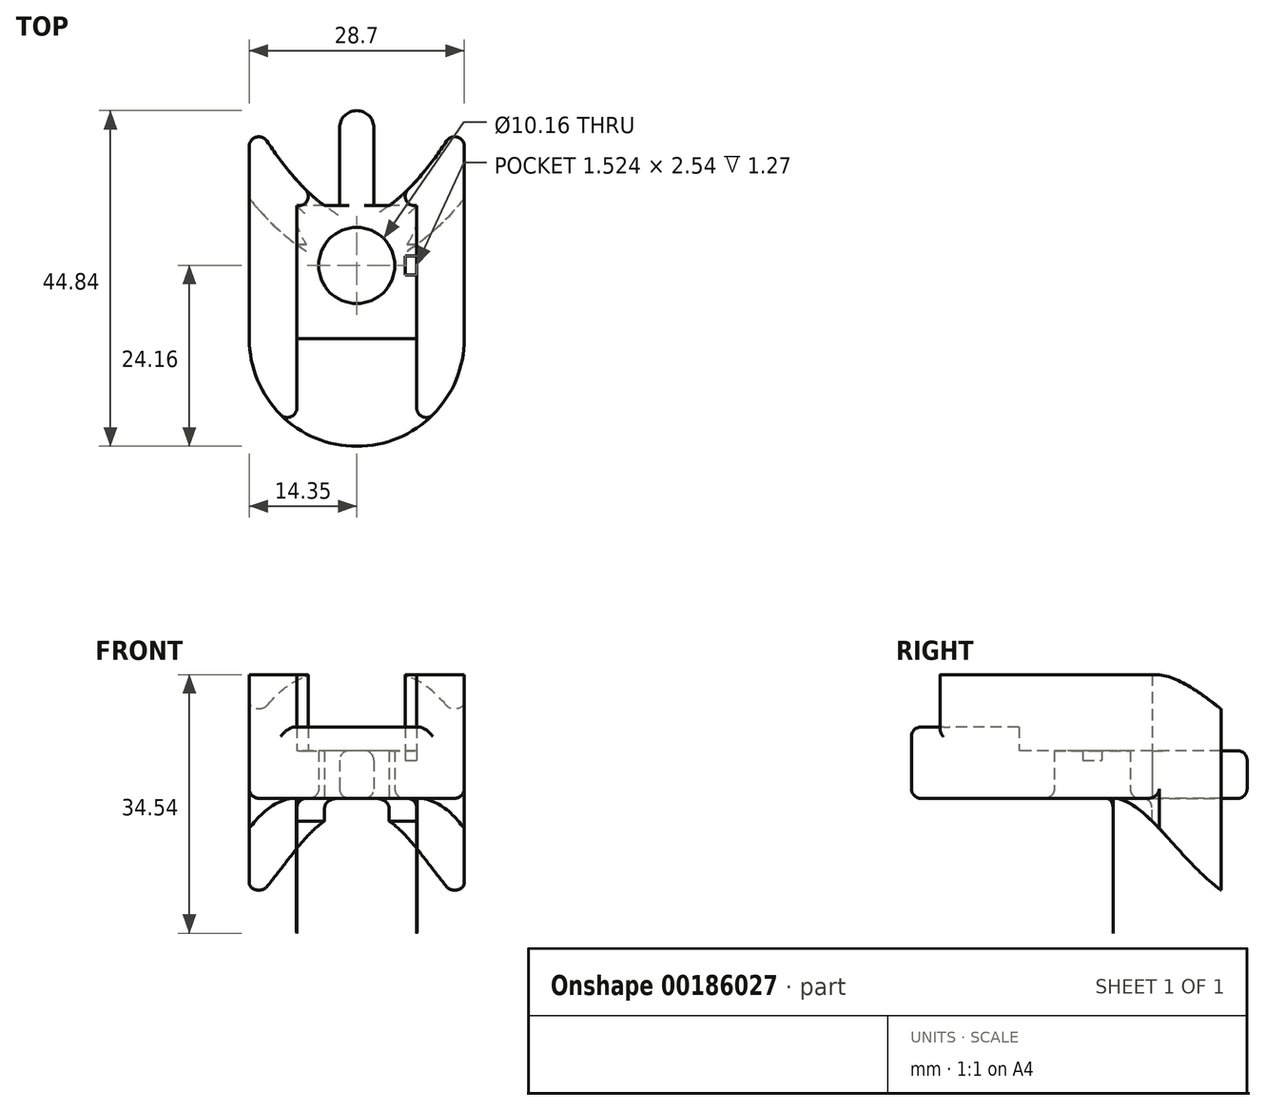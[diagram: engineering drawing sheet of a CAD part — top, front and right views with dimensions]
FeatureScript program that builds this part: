
annotation { "Feature Type Name" : "Feature", "Feature Type Description" : "" }
export const myFeature = defineFeature(function(context is Context, id is Id, definition is map)
    precondition{}
    {
        {
            var Q0;
            Q0=qCreatedBy(makeId("Top.planeOp"),FACE);
            var sketch = newSketch(context, id + "F0", { "sketchPlane" : qUnion([Q0])});
            skLineSegment(sketch, "E0", {"start": v(0, 45.72) * mm, "end": v(0, -45.72) * mm, "construction": true});
            skLineSegment(sketch, "E1", {"start": v(-22.35, 22.86) * mm, "end": v(22.35, 22.86) * mm, "construction": true});
            skLineSegment(sketch, "E2", {"start": v(-18.8, -22.86) * mm, "end": v(18.8, -22.86) * mm, "construction": true});
            skPoint(sketch, "E3", {"position": v(0, 22.86) * mm});
            skPoint(sketch, "E4", {"position": v(0, -22.86) * mm});
            skPoint(sketch, "E5", {"position": v(0, 0) * mm});
            skLineSegment(sketch, "E6", {"start": v(-24, 0) * mm, "end": v(24, 0) * mm, "construction": true});
            skFitSpline(sketch, "E7", {"points": [v(0, 45.72) * mm, v(-22.35, 22.86) * mm, v(-24, 0) * mm, v(-18.8, -22.86) * mm, v(0, -45.72) * mm], "startDerivative": vector(-139.64, 0) * mm, "endDerivative": vector(72.57, 0) * mm});
            skLineSegment(sketch, "E8", {"start": v(0, -45.72) * mm, "end": v(-6.35, -45.72) * mm, "construction": true});
            skLineSegment(sketch, "E9", {"start": v(-12.7, 45.72) * mm, "end": v(0, 45.72) * mm});
            skFitSpline(sketch, "E10.MirrorCS", {"points": [v(0, 45.72) * mm, v(22.35, 22.86) * mm, v(24, 0) * mm, v(18.8, -22.86) * mm, v(0, -45.72) * mm], "startDerivative": vector(139.64, 0) * mm, "endDerivative": vector(-72.57, 0) * mm});
            skFitSpline(sketch, "E11.0", {"points": [v(0, 52.07) * mm, v(-1.93, 52.07) * mm, v(-5.68, 51.63) * mm, v(-10.74, 49.77) * mm, v(-15.08, 47) * mm, v(-18.7, 43.6) * mm, v(-21.67, 39.8) * mm, v(-24.1, 35.77) * mm, v(-26.06, 31.63) * mm, v(-27.36, 28.19) * mm, v(-28.21, 25.5) * mm, v(-28.95, 22.86) * mm, v(-29.67, 19.67) * mm, v(-30.26, 16) * mm, v(-30.6, 12.49) * mm, v(-30.74, 9.12) * mm, v(-30.71, 5.9) * mm, v(-30.6, 3.32) * mm, v(-30.47, 1.33) * mm, v(-30.38, 0.1) * mm, v(-30.3, -0.86) * mm, v(-30.23, -1.83) * mm, v(-30.12, -3.05) * mm, v(-29.98, -4.54) * mm, v(-29.75, -6.56) * mm, v(-29.4, -9.16) * mm, v(-28.8, -12.4) * mm, v(-28, -15.78) * mm, v(-26.96, -19.32) * mm, v(-25.85, -22.4) * mm, v(-24.81, -24.96) * mm, v(-23.66, -27.59) * mm, v(-22.04, -30.96) * mm, v(-19.82, -35.02) * mm, v(-17.37, -38.97) * mm, v(-14.71, -42.67) * mm, v(-12.32, -45.47) * mm, v(-10.26, -47.47) * mm, v(-8.62, -48.84) * mm, v(-6.83, -50.07) * mm, v(-4.85, -51.1) * mm, v(-2.6, -51.86) * mm, v(-0.88, -52.07) * mm, v(0, -52.07) * mm]});
            skFitSpline(sketch, "E11.1", {"points": [v(0, 52.07) * mm, v(1.93, 52.07) * mm, v(5.68, 51.63) * mm, v(10.74, 49.77) * mm, v(15.08, 47) * mm, v(18.7, 43.6) * mm, v(21.67, 39.8) * mm, v(24.1, 35.77) * mm, v(26.06, 31.63) * mm, v(27.36, 28.19) * mm, v(28.21, 25.5) * mm, v(28.95, 22.86) * mm, v(29.67, 19.67) * mm, v(30.26, 16) * mm, v(30.6, 12.49) * mm, v(30.74, 9.12) * mm, v(30.71, 5.9) * mm, v(30.6, 3.32) * mm, v(30.47, 1.33) * mm, v(30.38, 0.1) * mm, v(30.3, -0.86) * mm, v(30.23, -1.83) * mm, v(30.12, -3.05) * mm, v(29.98, -4.54) * mm, v(29.75, -6.56) * mm, v(29.4, -9.16) * mm, v(28.8, -12.4) * mm, v(28, -15.78) * mm, v(26.96, -19.32) * mm, v(25.85, -22.4) * mm, v(24.81, -24.96) * mm, v(23.66, -27.59) * mm, v(22.04, -30.96) * mm, v(19.82, -35.02) * mm, v(17.37, -38.97) * mm, v(14.71, -42.67) * mm, v(12.32, -45.47) * mm, v(10.26, -47.47) * mm, v(8.62, -48.84) * mm, v(6.83, -50.07) * mm, v(4.85, -51.1) * mm, v(2.6, -51.86) * mm, v(0.88, -52.07) * mm, v(0, -52.07) * mm]});
            skLineSegment(sketch, "E12", {"start": v(-22.35, 22.86) * mm, "end": v(-30.27, 15.58) * mm});
            skLineSegment(sketch, "E13.MirrorCS", {"start": v(22.35, 22.86) * mm, "end": v(30.27, 15.58) * mm});
            skLineSegment(sketch, "E14.bottom", {"start": v(8, -44.1) * mm, "end": v(-8, -44.1) * mm});
            skLineSegment(sketch, "E14.top", {"start": v(8, -61.87) * mm, "end": v(-8, -61.87) * mm});
            skLineSegment(sketch, "E14.left", {"start": v(8, -44.1) * mm, "end": v(8, -61.87) * mm});
            skLineSegment(sketch, "E14.right", {"start": v(-8, -44.1) * mm, "end": v(-8, -61.87) * mm});
            skPoint(sketch, "E14.middle", {"position": v(0, -52.98) * mm});
            skCircle(sketch, "E15", {"center": v(0, -52.07) * mm, "radius": 5.08 * mm});
            skLineSegment(sketch, "E16", {"start": v(14.35, -31.7) * mm, "end": v(14.35, -61.87) * mm});
            skLineSegment(sketch, "E17", {"start": v(14.35, -61.87) * mm, "end": v(-14.35, -61.87) * mm, "construction": true});
            skLineSegment(sketch, "E18", {"start": v(-14.35, -61.87) * mm, "end": v(-14.35, -31.7) * mm});
            skArc(sketch, "E19", {"start": v(-14.35, -61.87) * mm, "mid": v(0, -76.23) * mm, "end": v(14.35, -61.87) * mm});
            skLineSegment(sketch, "E20", {"start": v(8, -61.87) * mm, "end": v(8, -73.79) * mm});
            skLineSegment(sketch, "E21", {"start": v(-8, -61.87) * mm, "end": v(-8, -73.79) * mm});
            skLineSegment(sketch, "E22", {"start": v(-2.29, -44.1) * mm, "end": v(-2.29, -33.68) * mm});
            skArc(sketch, "E23", {"start": v(-2.29, -33.68) * mm, "mid": v(0, -31.4) * mm, "end": v(2.29, -33.68) * mm});
            skLineSegment(sketch, "E24", {"start": v(2.29, -33.68) * mm, "end": v(2.29, -44.1) * mm});
            skLineSegment(sketch, "E25", {"start": v(-2.29, -33.68) * mm, "end": v(2.29, -33.68) * mm, "construction": true});
            skLineSegment(sketch, "E26", {"start": v(0, -52.07) * mm, "end": v(8, -52.07) * mm, "construction": true});
            skLineSegment(sketch, "E27.bottom", {"start": v(8, -50.8) * mm, "end": v(6.48, -50.8) * mm});
            skLineSegment(sketch, "E27.top", {"start": v(8, -53.34) * mm, "end": v(6.48, -53.34) * mm});
            skLineSegment(sketch, "E27.left", {"start": v(8, -50.8) * mm, "end": v(8, -53.34) * mm});
            skLineSegment(sketch, "E27.right", {"start": v(6.48, -50.8) * mm, "end": v(6.48, -53.34) * mm});
            skPoint(sketch, "E27.middle", {"position": v(7.24, -52.07) * mm});
            skSolve(sketch);
        }
        {
            var Q0;
            {var subQ0=sQuery(id+"F0.wireOp",EDGE,"E12");var subQ1=sQuery(id+"F0.wireOp",EDGE,"E7");var subQ2=makeQuery(id+"F0.imprint","INTERSECT",VERTEX,{"derivedFrom":[subQ1,subQ0]});Q0=makeQuery(id+"F0.imprint","IMPRINT",FACE,{"disambiguationData":[TD([[makeQuery(id+"F0.imprint","IMPRINT",EDGE,{"disambiguationData":[TD([[subQ2,-1.0]])],"derivedFrom":subQ1}),-1.0]])]});}
            var Q1;
            {var subQ3=sQuery(id+"F0.wireOp",EDGE,"E7");var subQ5=sQuery(id+"F0.wireOp",EDGE,"E18");var subQ6=makeQuery(id+"F0.imprint","INTERSECT",VERTEX,{"derivedFrom":[subQ3,subQ5]});Q1=makeQuery(id+"F0.imprint","IMPRINT",FACE,{"disambiguationData":[TD([[makeQuery(id+"F0.imprint","IMPRINT",EDGE,{"disambiguationData":[TD([[subQ6,-1.0]])],"derivedFrom":subQ3}),-1.0]])]});}
            var Q2;
            {var subQ0=sQuery(id+"F0.wireOp",EDGE,"E13.MirrorCS");var subQ1=sQuery(id+"F0.wireOp",EDGE,"E10.MirrorCS");var subQ2=makeQuery(id+"F0.imprint","INTERSECT",VERTEX,{"derivedFrom":[subQ1,subQ0]});Q2=makeQuery(id+"F0.imprint","IMPRINT",FACE,{"disambiguationData":[TD([[makeQuery(id+"F0.imprint","IMPRINT",EDGE,{"disambiguationData":[TD([[subQ2,-1.0]])],"derivedFrom":subQ1}),1.0]])]});}
            var Q3;
            {var subQ5=sQuery(id+"F0.wireOp",EDGE,"E16");var subQ6=sQuery(id+"F0.wireOp",EDGE,"E10.MirrorCS");var subQ7=makeQuery(id+"F0.imprint","INTERSECT",VERTEX,{"derivedFrom":[subQ6,subQ5]});Q3=makeQuery(id+"F0.imprint","IMPRINT",FACE,{"disambiguationData":[TD([[makeQuery(id+"F0.imprint","IMPRINT",EDGE,{"disambiguationData":[TD([[subQ7,-1.0]])],"derivedFrom":subQ6}),1.0]])]});}
            var Q4;
            {var subQ3=sQuery(id+"F0.wireOp",EDGE,"E20");Q4=makeQuery(id+"F0.imprint","IMPRINT",FACE,{"disambiguationData":[TD([[makeQuery(id+"F0.imprint","IMPRINT",EDGE,{"derivedFrom":subQ3}),1.0]])]});}
            var Q5;
            {var subQ3=sQuery(id+"F0.wireOp",EDGE,"E21");Q5=makeQuery(id+"F0.imprint","IMPRINT",FACE,{"disambiguationData":[TD([[makeQuery(id+"F0.imprint","IMPRINT",EDGE,{"derivedFrom":subQ3}),-1.0]])]});}
            var Q6;
            {var subQ5=sQuery(id+"F0.wireOp",EDGE,"E10.MirrorCS");var subQ6=sQuery(id+"F0.wireOp",EDGE,"E7");var subQ7=makeQuery(id+"F0.imprint","INTERSECT",VERTEX,{"disambiguationData":[OD(1.0)],"derivedFrom":[subQ6,subQ5]});Q6=makeQuery(id+"F0.imprint","IMPRINT",FACE,{"disambiguationData":[TD([[makeQuery(id+"F0.imprint","IMPRINT",EDGE,{"disambiguationData":[TD([[subQ7,1.0]])],"derivedFrom":subQ6}),-1.0]])]});}
            var Q7;
            {var subQ0=sQuery(id+"F0.wireOp",EDGE,"E14.top");Q7=makeQuery(id+"F0.imprint","IMPRINT",FACE,{"disambiguationData":[TD([[makeQuery(id+"F0.imprint","IMPRINT",EDGE,{"derivedFrom":subQ0}),-1.0]])]});}
            var Q8;
            Q8=makeQuery(id+"F0.imprint","IMPRINT",FACE,{"disambiguationData":[TD([[makeQuery(id+"F0.imprint","IMPRINT",EDGE,{"derivedFrom":sQuery(id+"F0.wireOp",EDGE,"E14.top")}),1.0]])]});
            var Q9;
            {var subQ0=sQuery(id+"F0.wireOp",EDGE,"E10.MirrorCS");var subQ1=sQuery(id+"F0.wireOp",EDGE,"E7");var subQ2=makeQuery(id+"F0.imprint","INTERSECT",VERTEX,{"disambiguationData":[OD(1.0)],"derivedFrom":[subQ1,subQ0]});Q9=makeQuery(id+"F0.imprint","IMPRINT",FACE,{"disambiguationData":[TD([[makeQuery(id+"F0.imprint","IMPRINT",EDGE,{"disambiguationData":[TD([[subQ2,1.0]])],"derivedFrom":subQ1}),1.0]])]});}
            var Q10;
            {var subQ0=sQuery(id+"F0.wireOp",EDGE,"E22");Q10=makeQuery(id+"F0.imprint","IMPRINT",FACE,{"disambiguationData":[TD([[makeQuery(id+"F0.imprint","IMPRINT",EDGE,{"derivedFrom":subQ0}),-1.0]])]});}
            var Q11;
            Q11=makeQuery(id+"F0.imprint","IMPRINT",FACE,{"disambiguationData":[TD([[makeQuery(id+"F0.imprint","IMPRINT",EDGE,{"derivedFrom":sQuery(id+"F0.wireOp",EDGE,"E27.bottom")}),1.0]])]});
            extrude(context, id + "F1", {"entities" : qUnion([Q0, Q1, Q2, Q3, Q4, Q5, Q6, Q7, Q8, Q9, Q10, Q11]), "depth" : 5.08 * mm});
        }
        {
            var Q0;
            {var subQ7=sQuery(id+"F0.wireOp",EDGE,"E14.top");Q0=makeQuery(id+"F0.imprint","IMPRINT",FACE,{"disambiguationData":[TD([[makeQuery(id+"F0.imprint","IMPRINT",EDGE,{"derivedFrom":subQ7}),-1.0]])]});}
            var Q1;
            {var subQ5=sQuery(id+"F0.wireOp",EDGE,"E10.MirrorCS");var subQ6=sQuery(id+"F0.wireOp",EDGE,"E7");var subQ7=makeQuery(id+"F0.imprint","INTERSECT",VERTEX,{"disambiguationData":[OD(1.0)],"derivedFrom":[subQ6,subQ5]});Q1=makeQuery(id+"F0.imprint","IMPRINT",FACE,{"disambiguationData":[TD([[makeQuery(id+"F0.imprint","IMPRINT",EDGE,{"disambiguationData":[TD([[subQ7,1.0]])],"derivedFrom":subQ6}),-1.0]])]});}
            var Q2;
            {var subQ0=sQuery(id+"F0.wireOp",EDGE,"E22");Q2=makeQuery(id+"F0.imprint","IMPRINT",FACE,{"disambiguationData":[TD([[makeQuery(id+"F0.imprint","IMPRINT",EDGE,{"derivedFrom":subQ0}),-1.0]])]});}
            var Q3;
            {var subQ3=sQuery(id+"F0.wireOp",EDGE,"E7");var subQ5=sQuery(id+"F0.wireOp",EDGE,"E10.MirrorCS");var subQ7=makeQuery(id+"F0.imprint","INTERSECT",VERTEX,{"disambiguationData":[OD(1.0)],"derivedFrom":[subQ3,subQ5]});Q3=makeQuery(id+"F0.imprint","IMPRINT",FACE,{"disambiguationData":[TD([[makeQuery(id+"F0.imprint","IMPRINT",EDGE,{"disambiguationData":[TD([[subQ7,1.0]])],"derivedFrom":subQ3}),1.0]])]});}
            extrude(context, id + "F2", {"entities" : qUnion([Q0, Q1, Q2, Q3]), "operationType" : NewBodyOperationType.ADD, "depth" : 6.35 * mm});
        }
        {
            var Q0;
            Q0=makeQuery(id+"F0.imprint","IMPRINT",FACE,{"disambiguationData":[TD([[makeQuery(id+"F0.imprint","IMPRINT",EDGE,{"derivedFrom":sQuery(id+"F0.wireOp",EDGE,"E14.top")}),1.0]])]});
            extrude(context, id + "F3", {"entities" : qUnion([Q0]), "operationType" : NewBodyOperationType.ADD, "depth" : 9.52 * mm});
        }
        {
            var Q0;
            {var subQ5=sQuery(id+"F0.wireOp",EDGE,"E20");Q0=makeQuery(id+"F0.imprint","IMPRINT",FACE,{"disambiguationData":[TD([[makeQuery(id+"F0.imprint","IMPRINT",EDGE,{"derivedFrom":subQ5}),1.0]])]});}
            var Q1;
            {var subQ5=sQuery(id+"F0.wireOp",EDGE,"E16");var subQ7=sQuery(id+"F0.wireOp",EDGE,"E10.MirrorCS");var subQ9=makeQuery(id+"F0.imprint","INTERSECT",VERTEX,{"derivedFrom":[subQ7,subQ5]});Q1=makeQuery(id+"F0.imprint","IMPRINT",FACE,{"disambiguationData":[TD([[makeQuery(id+"F0.imprint","IMPRINT",EDGE,{"disambiguationData":[TD([[subQ9,-1.0]])],"derivedFrom":subQ7}),1.0]])]});}
            var Q2;
            {var subQ3=sQuery(id+"F0.wireOp",EDGE,"E21");Q2=makeQuery(id+"F0.imprint","IMPRINT",FACE,{"disambiguationData":[TD([[makeQuery(id+"F0.imprint","IMPRINT",EDGE,{"derivedFrom":subQ3}),-1.0]])]});}
            var Q3;
            {var subQ5=sQuery(id+"F0.wireOp",EDGE,"E18");var subQ6=sQuery(id+"F0.wireOp",EDGE,"E7");var subQ7=makeQuery(id+"F0.imprint","INTERSECT",VERTEX,{"derivedFrom":[subQ6,subQ5]});Q3=makeQuery(id+"F0.imprint","IMPRINT",FACE,{"disambiguationData":[TD([[makeQuery(id+"F0.imprint","IMPRINT",EDGE,{"disambiguationData":[TD([[subQ7,-1.0]])],"derivedFrom":subQ6}),-1.0]])]});}
            extrude(context, id + "F4", {"entities" : qUnion([Q0, Q1, Q2, Q3]), "operationType" : NewBodyOperationType.ADD, "depth" : 16.5 * mm});
        }
        {
            var Q0;
            {var subQ5=sQuery(id+"F0.wireOp",EDGE,"E18");var subQ6=sQuery(id+"F0.wireOp",EDGE,"E7");var subQ7=makeQuery(id+"F0.imprint","INTERSECT",VERTEX,{"derivedFrom":[subQ6,subQ5]});Q0=makeQuery(id+"F0.imprint","IMPRINT",FACE,{"disambiguationData":[TD([[makeQuery(id+"F0.imprint","IMPRINT",EDGE,{"disambiguationData":[TD([[subQ7,-1.0]])],"derivedFrom":subQ6}),-1.0]])]});}
            var Q1;
            {var subQ0=sQuery(id+"F0.wireOp",EDGE,"E12");var subQ1=sQuery(id+"F0.wireOp",EDGE,"E7");var subQ2=makeQuery(id+"F0.imprint","INTERSECT",VERTEX,{"derivedFrom":[subQ1,subQ0]});Q1=makeQuery(id+"F0.imprint","IMPRINT",FACE,{"disambiguationData":[TD([[makeQuery(id+"F0.imprint","IMPRINT",EDGE,{"disambiguationData":[TD([[subQ2,-1.0]])],"derivedFrom":subQ1}),-1.0]])]});}
            var Q2;
            {var subQ5=sQuery(id+"F0.wireOp",EDGE,"E16");var subQ7=sQuery(id+"F0.wireOp",EDGE,"E10.MirrorCS");var subQ9=makeQuery(id+"F0.imprint","INTERSECT",VERTEX,{"derivedFrom":[subQ7,subQ5]});Q2=makeQuery(id+"F0.imprint","IMPRINT",FACE,{"disambiguationData":[TD([[makeQuery(id+"F0.imprint","IMPRINT",EDGE,{"disambiguationData":[TD([[subQ9,-1.0]])],"derivedFrom":subQ7}),1.0]])]});}
            var Q3;
            {var subQ0=sQuery(id+"F0.wireOp",EDGE,"E13.MirrorCS");var subQ1=sQuery(id+"F0.wireOp",EDGE,"E10.MirrorCS");var subQ2=makeQuery(id+"F0.imprint","INTERSECT",VERTEX,{"derivedFrom":[subQ1,subQ0]});Q3=makeQuery(id+"F0.imprint","IMPRINT",FACE,{"disambiguationData":[TD([[makeQuery(id+"F0.imprint","IMPRINT",EDGE,{"disambiguationData":[TD([[subQ2,-1.0]])],"derivedFrom":subQ1}),1.0]])]});}
            extrude(context, id + "F5", {"entities" : qUnion([Q0, Q1, Q2, Q3]), "operationType" : NewBodyOperationType.ADD, "oppositeDirection" : true, "depth" : 19.05 * mm, "hasSecondDirection" : true, "secondDirectionOppositeDirection" : false, "secondDirectionDepth" : 16.5 * mm});
        }
        {
            var Q0;
            Q0=qCreatedBy(makeId("Right.planeOp"),FACE);
            var sketch = newSketch(context, id + "F6", { "sketchPlane" : qUnion([Q0])});
            skFitSpline(sketch, "E28", {"points": [v(-49.27, 0) * mm, v(-40.72, -6.68) * mm, v(-32.49, -13.94) * mm, v(-17.05, -19.05) * mm], "startDerivative": vector(27.03, 0) * mm, "endDerivative": vector(45.72, -0.93) * mm});
            skFitSpline(sketch, "E29", {"points": [v(-11.78, 0) * mm, v(-29.9, 7.9) * mm, v(-43.68, 16.51) * mm], "startDerivative": vector(-38.45, 0) * mm, "endDerivative": vector(-24.58, 0) * mm});
            skLineSegment(sketch, "E30", {"start": v(-43.68, 16.51) * mm, "end": v(22.86, 16.51) * mm});
            skLineSegment(sketch, "E31", {"start": v(22.86, 16.51) * mm, "end": v(22.86, 0) * mm});
            skLineSegment(sketch, "E32", {"start": v(22.86, 0) * mm, "end": v(-11.78, 0) * mm});
            skLineSegment(sketch, "E33", {"start": v(-49.27, 0) * mm, "end": v(-49.27, -19.05) * mm});
            skLineSegment(sketch, "E34", {"start": v(-49.27, -19.05) * mm, "end": v(-17.05, -19.05) * mm});
            skSolve(sketch);
        }
        {
            var Q0;
            Q0=makeQuery(id+"F6.imprint","IMPRINT",FACE,{"disambiguationData":[TD([[makeQuery(id+"F6.imprint","IMPRINT",EDGE,{"derivedFrom":sQuery(id+"F6.wireOp",EDGE,"E29")}),-1.0]])]});
            var Q1;
            Q1=makeQuery(id+"F6.imprint","IMPRINT",FACE,{"disambiguationData":[TD([[makeQuery(id+"F6.imprint","IMPRINT",EDGE,{"derivedFrom":sQuery(id+"F6.wireOp",EDGE,"E28")}),-1.0]])]});
            extrude(context, id + "F7", {"entities" : qUnion([Q0, Q1]), "operationType" : NewBodyOperationType.REMOVE, "endBound" : BoundingType.THROUGH_ALL, "oppositeDirection" : true, "depth" : 50.8 * mm, "hasSecondDirection" : true, "secondDirectionBound" : SecondDirectionBoundingType.THROUGH_ALL, "secondDirectionOppositeDirection" : false, "secondDirectionDepth" : 25.4 * mm});
        }
        {
            var Q0;
            {var subQ0=sQuery(id+"F0.wireOp",EDGE,"be17f513-7395-4ca1-bee9-ffb8ea424e3f");Q0=makeQuery(id+"F7.boolean.opBoolean","INTERSECT",EDGE,{"derivedFrom":[makeQuery(id+"F5.boolean.opBoolean","MERGE",FACE,{"derivedFrom":[makeQuery(id+"F4.boolean.opBoolean","MERGE",FACE,{"derivedFrom":[makeQuery(id+"F3.boolean.opBoolean","MERGE",FACE,{"derivedFrom":[makeQuery(id+"F1.opExtrude","SWEPT_FACE",FACE,{"disambiguationData":[OSD([subQ0])]}),makeQuery(id+"F3.opExtrude","SWEPT_FACE",FACE,{"disambiguationData":[OSD([subQ0])]})]}),makeQuery(id+"F4.opExtrude","SWEPT_FACE",FACE,{"disambiguationData":[OSD([subQ0])]})]}),makeQuery(id+"F5.opExtrude","SWEPT_FACE",FACE,{"disambiguationData":[OSD([subQ0])]})]}),makeQuery(id+"F7.opExtrude","SWEPT_FACE",FACE,{"disambiguationData":[OSD([sQuery(id+"F6.wireOp",EDGE,"E29")])]})]});}
            var Q1;
            {var subQ0=sQuery(id+"F0.wireOp",EDGE,"43ab01d4-1301-4dd6-aa0a-0130827a8f120.MirrorCS");Q1=makeQuery(id+"F7.boolean.opBoolean","INTERSECT",EDGE,{"derivedFrom":[makeQuery(id+"F5.boolean.opBoolean","MERGE",FACE,{"derivedFrom":[makeQuery(id+"F4.boolean.opBoolean","MERGE",FACE,{"derivedFrom":[makeQuery(id+"F3.boolean.opBoolean","MERGE",FACE,{"derivedFrom":[makeQuery(id+"F1.opExtrude","SWEPT_FACE",FACE,{"disambiguationData":[OSD([subQ0])]}),makeQuery(id+"F3.opExtrude","SWEPT_FACE",FACE,{"disambiguationData":[OSD([subQ0])]})]}),makeQuery(id+"F4.opExtrude","SWEPT_FACE",FACE,{"disambiguationData":[OSD([subQ0])]})]}),makeQuery(id+"F5.opExtrude","SWEPT_FACE",FACE,{"disambiguationData":[OSD([subQ0])]})]}),makeQuery(id+"F7.opExtrude","SWEPT_FACE",FACE,{"disambiguationData":[OSD([sQuery(id+"F6.wireOp",EDGE,"E29")])]})]});}
            var Q2;
            {var subQ0=sQuery(id+"F0.wireOp",EDGE,"ee3d559f-ee6a-4725-bef5-1b4b77159640.1");Q2=makeQuery(id+"F7.boolean.opBoolean","INTERSECT",EDGE,{"derivedFrom":[makeQuery(id+"F5.boolean.opBoolean","MERGE",FACE,{"derivedFrom":[makeQuery(id+"F1.opExtrude","SWEPT_FACE",FACE,{"disambiguationData":[OSD([subQ0])]}),makeQuery(id+"F5.opExtrude","SWEPT_FACE",FACE,{"disambiguationData":[OSD([subQ0])]})]}),makeQuery(id+"F7.opExtrude","SWEPT_FACE",FACE,{"disambiguationData":[OSD([sQuery(id+"F6.wireOp",EDGE,"E29")])]})]});}
            var Q3;
            {var subQ0=sQuery(id+"F0.wireOp",EDGE,"ee3d559f-ee6a-4725-bef5-1b4b77159640.0");Q3=makeQuery(id+"F7.boolean.opBoolean","INTERSECT",EDGE,{"derivedFrom":[makeQuery(id+"F5.boolean.opBoolean","MERGE",FACE,{"derivedFrom":[makeQuery(id+"F1.opExtrude","SWEPT_FACE",FACE,{"disambiguationData":[OSD([subQ0])]}),makeQuery(id+"F5.opExtrude","SWEPT_FACE",FACE,{"disambiguationData":[OSD([subQ0])]})]}),makeQuery(id+"F7.opExtrude","SWEPT_FACE",FACE,{"disambiguationData":[OSD([sQuery(id+"F6.wireOp",EDGE,"E29")])]})]});}
            var Q4;
            {var subQ0=sQuery(id+"F0.wireOp",EDGE,"ee3d559f-ee6a-4725-bef5-1b4b77159640.1");Q4=makeQuery(id+"F7.boolean.opBoolean","INTERSECT",EDGE,{"derivedFrom":[makeQuery(id+"F5.boolean.opBoolean","MERGE",FACE,{"derivedFrom":[makeQuery(id+"F1.opExtrude","SWEPT_FACE",FACE,{"disambiguationData":[OSD([subQ0])]}),makeQuery(id+"F5.opExtrude","SWEPT_FACE",FACE,{"disambiguationData":[OSD([subQ0])]})]}),makeQuery(id+"F7.opExtrude","SWEPT_FACE",FACE,{"disambiguationData":[OSD([sQuery(id+"F6.wireOp",EDGE,"E28")])]})]});}
            var Q5;
            {var subQ0=sQuery(id+"F0.wireOp",EDGE,"ee3d559f-ee6a-4725-bef5-1b4b77159640.0");Q5=makeQuery(id+"F7.boolean.opBoolean","INTERSECT",EDGE,{"derivedFrom":[makeQuery(id+"F5.boolean.opBoolean","MERGE",FACE,{"derivedFrom":[makeQuery(id+"F1.opExtrude","SWEPT_FACE",FACE,{"disambiguationData":[OSD([subQ0])]}),makeQuery(id+"F5.opExtrude","SWEPT_FACE",FACE,{"disambiguationData":[OSD([subQ0])]})]}),makeQuery(id+"F7.opExtrude","SWEPT_FACE",FACE,{"disambiguationData":[OSD([sQuery(id+"F6.wireOp",EDGE,"E28")])]})]});}
            var Q6;
            {var subQ1=sQuery(id+"F0.wireOp",EDGE,"43ab01d4-1301-4dd6-aa0a-0130827a8f120.MirrorCS");Q6=makeQuery(id+"F7.boolean.opBoolean","COPY",FACE,{"disambiguationData":[TD([makeQuery(id+"F1.opExtrude","SWEPT_FACE",FACE,{"disambiguationData":[OSD([subQ1])]})])],"derivedFrom":makeQuery(id+"F7.opExtrude","SWEPT_FACE",FACE,{"disambiguationData":[OSD([sQuery(id+"F6.wireOp",EDGE,"E28")])]})});}
            var Q7;
            {var subQ1=sQuery(id+"F0.wireOp",EDGE,"be17f513-7395-4ca1-bee9-ffb8ea424e3f");Q7=makeQuery(id+"F7.boolean.opBoolean","COPY",FACE,{"disambiguationData":[TD([makeQuery(id+"F1.opExtrude","SWEPT_FACE",FACE,{"disambiguationData":[OSD([subQ1])]})])],"derivedFrom":makeQuery(id+"F7.opExtrude","SWEPT_FACE",FACE,{"disambiguationData":[OSD([sQuery(id+"F6.wireOp",EDGE,"E28")])]})});}
            var Q8;
            Q8=makeQuery(id+"F5.opExtrude","CAP_FACE",FACE,{"disambiguationData":[OSD([sQuery(id+"F0.wireOp",EDGE,"be17f513-7395-4ca1-bee9-ffb8ea424e3f"),sQuery(id+"F0.wireOp",EDGE,"ee3d559f-ee6a-4725-bef5-1b4b77159640.0"),sQuery(id+"F0.wireOp",EDGE,"68642bd1-f1df-4fe3-9d6f-ef0b44e5282e0.MirrorCS"),sQuery(id+"F0.wireOp",EDGE,"7FS2mD8Q-LMsh-AhyU-2CDM-JIsEHGZjZGS2.right"),sQuery(id+"F0.wireOp",EDGE,"OyAj4o25-fk0b-uL6F-qYXP-0dRr7gncsmqc")])],"isStart":false});
            var Q9;
            Q9=makeQuery(id+"F5.opExtrude","CAP_FACE",FACE,{"disambiguationData":[OSD([sQuery(id+"F0.wireOp",EDGE,"43ab01d4-1301-4dd6-aa0a-0130827a8f120.MirrorCS"),sQuery(id+"F0.wireOp",EDGE,"ee3d559f-ee6a-4725-bef5-1b4b77159640.1"),sQuery(id+"F0.wireOp",EDGE,"CaFeobp9-MKSn-WcLS-xQQh-gSaBlFYCHn7S"),sQuery(id+"F0.wireOp",EDGE,"7FS2mD8Q-LMsh-AhyU-2CDM-JIsEHGZjZGS2.left"),sQuery(id+"F0.wireOp",EDGE,"qwDXIH1N-C4LK-unpw-krAA-JUrWlVBK7Anx")])],"isStart":false});
            var Q10;
            {var subQ0=sQuery(id+"F0.wireOp",EDGE,"68642bd1-f1df-4fe3-9d6f-ef0b44e5282e0.MirrorCS");Q10=makeQuery(id+"F5.boolean.opBoolean","MERGE",FACE,{"derivedFrom":[makeQuery(id+"F1.opExtrude","SWEPT_FACE",FACE,{"disambiguationData":[OSD([subQ0])]}),makeQuery(id+"F5.opExtrude","SWEPT_FACE",FACE,{"disambiguationData":[OSD([subQ0])]})]});}
            var Q11;
            {var subQ0=sQuery(id+"F0.wireOp",EDGE,"CaFeobp9-MKSn-WcLS-xQQh-gSaBlFYCHn7S");Q11=makeQuery(id+"F5.boolean.opBoolean","MERGE",FACE,{"derivedFrom":[makeQuery(id+"F1.opExtrude","SWEPT_FACE",FACE,{"disambiguationData":[OSD([subQ0])]}),makeQuery(id+"F5.opExtrude","SWEPT_FACE",FACE,{"disambiguationData":[OSD([subQ0])]})]});}
            var Q12;
            {var subQ0=sQuery(id+"F0.wireOp",EDGE,"7FS2mD8Q-LMsh-AhyU-2CDM-JIsEHGZjZGS2.bottom");var subQ1=sQuery(id+"F0.wireOp",EDGE,"43ab01d4-1301-4dd6-aa0a-0130827a8f120.MirrorCS");Q12=makeQuery(id+"F4.boolean.opBoolean","MERGE",EDGE,{"derivedFrom":[makeQuery(id+"F3.boolean.opBoolean","SPLIT",EDGE,{"derivedFrom":makeQuery(id+"F3.opExtrude","SWEPT_EDGE",EDGE,{"disambiguationData":[OSD([subQ1,subQ0])]})}),makeQuery(id+"F4.opExtrude","SWEPT_EDGE",EDGE,{"disambiguationData":[OSD([subQ1,subQ0])]})]});}
            var Q13;
            {var subQ0=sQuery(id+"F0.wireOp",EDGE,"7FS2mD8Q-LMsh-AhyU-2CDM-JIsEHGZjZGS2.bottom");var subQ1=sQuery(id+"F0.wireOp",EDGE,"be17f513-7395-4ca1-bee9-ffb8ea424e3f");Q13=makeQuery(id+"F4.boolean.opBoolean","MERGE",EDGE,{"derivedFrom":[makeQuery(id+"F3.boolean.opBoolean","SPLIT",EDGE,{"derivedFrom":makeQuery(id+"F3.opExtrude","SWEPT_EDGE",EDGE,{"disambiguationData":[OSD([subQ1,subQ0])]})}),makeQuery(id+"F4.opExtrude","SWEPT_EDGE",EDGE,{"disambiguationData":[OSD([subQ1,subQ0])]})]});}
            var Q14;
            Q14=makeQuery(id+"F5.opExtrude","CAP_EDGE",EDGE,{"disambiguationData":[OSD([sQuery(id+"F0.wireOp",EDGE,"E12")])],"isStart":false});
            var Q15;
            Q15=makeQuery(id+"F5.opExtrude","CAP_EDGE",EDGE,{"disambiguationData":[OSD([sQuery(id+"F0.wireOp",EDGE,"E13.MirrorCS")])],"isStart":false});
            var Q16;
            Q16=makeQuery(id+"F5.opExtrude","CAP_EDGE",EDGE,{"disambiguationData":[OSD([sQuery(id+"F0.wireOp",EDGE,"E11.1")])],"isStart":false});
            var Q17;
            Q17=makeQuery(id+"F5.opExtrude","CAP_EDGE",EDGE,{"disambiguationData":[OSD([sQuery(id+"F0.wireOp",EDGE,"E11.0")])],"isStart":false});
            var Q18;
            Q18=makeQuery(id+"F5.opExtrude","CAP_EDGE",EDGE,{"disambiguationData":[OSD([sQuery(id+"F0.wireOp",EDGE,"E7")])],"isStart":false});
            var Q19;
            Q19=makeQuery(id+"F5.opExtrude","CAP_EDGE",EDGE,{"disambiguationData":[OSD([sQuery(id+"F0.wireOp",EDGE,"E10.MirrorCS")])],"isStart":false});
            var Q20;
            {var subQ0=sQuery(id+"F0.wireOp",EDGE,"E12");Q20=makeQuery(id+"F7.boolean.opBoolean","INTERSECT",EDGE,{"derivedFrom":[makeQuery(id+"F5.boolean.opBoolean","MERGE",FACE,{"derivedFrom":[makeQuery(id+"F1.opExtrude","SWEPT_FACE",FACE,{"disambiguationData":[OSD([subQ0])]}),makeQuery(id+"F5.opExtrude","SWEPT_FACE",FACE,{"disambiguationData":[OSD([subQ0])]})]}),makeQuery(id+"F7.opExtrude","SWEPT_FACE",FACE,{"disambiguationData":[OSD([sQuery(id+"F6.wireOp",EDGE,"E32")])]})]});}
            var Q21;
            {var subQ0=sQuery(id+"F0.wireOp",EDGE,"E13.MirrorCS");Q21=makeQuery(id+"F7.boolean.opBoolean","INTERSECT",EDGE,{"derivedFrom":[makeQuery(id+"F5.boolean.opBoolean","MERGE",FACE,{"derivedFrom":[makeQuery(id+"F1.opExtrude","SWEPT_FACE",FACE,{"disambiguationData":[OSD([subQ0])]}),makeQuery(id+"F5.opExtrude","SWEPT_FACE",FACE,{"disambiguationData":[OSD([subQ0])]})]}),makeQuery(id+"F7.opExtrude","SWEPT_FACE",FACE,{"disambiguationData":[OSD([sQuery(id+"F6.wireOp",EDGE,"E32")])]})]});}
            var Q22;
            {var subQ0=sQuery(id+"F0.wireOp",EDGE,"E12");var subQ1=sQuery(id+"F0.wireOp",EDGE,"E11.0");Q22=makeQuery(id+"F5.boolean.opBoolean","MERGE",EDGE,{"derivedFrom":[makeQuery(id+"F1.opExtrude","SWEPT_EDGE",EDGE,{"disambiguationData":[OSD([subQ1,subQ0])]}),makeQuery(id+"F5.opExtrude","SWEPT_EDGE",EDGE,{"disambiguationData":[OSD([subQ1,subQ0])]})]});}
            var Q23;
            {var subQ0=sQuery(id+"F0.wireOp",EDGE,"E13.MirrorCS");var subQ1=sQuery(id+"F0.wireOp",EDGE,"E11.1");Q23=makeQuery(id+"F5.boolean.opBoolean","MERGE",EDGE,{"derivedFrom":[makeQuery(id+"F1.opExtrude","SWEPT_EDGE",EDGE,{"disambiguationData":[OSD([subQ1,subQ0])]}),makeQuery(id+"F5.opExtrude","SWEPT_EDGE",EDGE,{"disambiguationData":[OSD([subQ1,subQ0])]})]});}
            var Q24;
            {var subQ0=sQuery(id+"F0.wireOp",EDGE,"E12");var subQ1=sQuery(id+"F0.wireOp",EDGE,"E7");Q24=makeQuery(id+"F5.boolean.opBoolean","MERGE",EDGE,{"derivedFrom":[makeQuery(id+"F1.opExtrude","SWEPT_EDGE",EDGE,{"disambiguationData":[OSD([subQ1,subQ0])]}),makeQuery(id+"F5.opExtrude","SWEPT_EDGE",EDGE,{"disambiguationData":[OSD([subQ1,subQ0])]})]});}
            var Q25;
            {var subQ0=sQuery(id+"F0.wireOp",EDGE,"E13.MirrorCS");var subQ1=sQuery(id+"F0.wireOp",EDGE,"E10.MirrorCS");Q25=makeQuery(id+"F5.boolean.opBoolean","MERGE",EDGE,{"derivedFrom":[makeQuery(id+"F1.opExtrude","SWEPT_EDGE",EDGE,{"disambiguationData":[OSD([subQ1,subQ0])]}),makeQuery(id+"F5.opExtrude","SWEPT_EDGE",EDGE,{"disambiguationData":[OSD([subQ1,subQ0])]})]});}
            fillet(context, id + "F8", {"entities" : qUnion([Q0, Q1, Q2, Q3, Q4, Q5, Q6, Q7, Q8, Q9, Q10, Q11, Q12, Q13, Q14, Q15, Q16, Q17, Q18, Q19, Q20, Q21, Q22, Q23, Q24, Q25]), "radius" : 1.27 * mm, "tangentPropagation" : true, "allowEdgeOverflow" : false});
        }
        {
            var Q0;
            Q0=makeQuery(id+"F1.opExtrude","CAP_EDGE",EDGE,{"disambiguationData":[OSD([sQuery(id+"F0.wireOp",EDGE,"E22")])],"isStart":true});
            var Q1;
            Q1=makeQuery(id+"F2.opExtrude","CAP_EDGE",EDGE,{"disambiguationData":[OSD([sQuery(id+"F0.wireOp",EDGE,"E22")])],"isStart":false});
            fillet(context, id + "F9", {"entities" : qUnion([Q0, Q1]), "radius" : 1.27 * mm, "tangentPropagation" : true, "allowEdgeOverflow" : false});
        }
        {
            var Q0;
            Q0=makeQuery(id+"F1.opExtrude","CAP_EDGE",EDGE,{"disambiguationData":[OSD([sQuery(id+"F0.wireOp",EDGE,"E18")])],"isStart":true});
            var Q1;
            Q1=makeQuery(id+"F1.opExtrude","CAP_EDGE",EDGE,{"disambiguationData":[OSD([sQuery(id+"F0.wireOp",EDGE,"E15")])],"isStart":true});
            var Q2;
            Q2=makeQuery(id+"F5.boolean.opBoolean","INTERSECT",EDGE,{"derivedFrom":[makeQuery(id+"F1.opExtrude","CAP_FACE",FACE,{"disambiguationData":[OSD([sQuery(id+"F0.wireOp",EDGE,"E7"),sQuery(id+"F0.wireOp",EDGE,"E10.MirrorCS"),sQuery(id+"F0.wireOp",EDGE,"E11.0"),sQuery(id+"F0.wireOp",EDGE,"E11.1"),sQuery(id+"F0.wireOp",EDGE,"E12"),sQuery(id+"F0.wireOp",EDGE,"E13.MirrorCS"),sQuery(id+"F0.wireOp",EDGE,"E14.bottom"),sQuery(id+"F0.wireOp",EDGE,"E15"),sQuery(id+"F0.wireOp",EDGE,"E16"),sQuery(id+"F0.wireOp",EDGE,"E18"),sQuery(id+"F0.wireOp",EDGE,"E19"),sQuery(id+"F0.wireOp",EDGE,"E22"),sQuery(id+"F0.wireOp",EDGE,"E23"),sQuery(id+"F0.wireOp",EDGE,"E24")])],"isStart":true}),makeQuery(id+"F5.opExtrude","SWEPT_FACE",FACE,{"disambiguationData":[OSD([sQuery(id+"F0.wireOp",EDGE,"E14.right")])]})]});
            var Q3;
            {var subQ0=sQuery(id+"F0.wireOp",EDGE,"E14.bottom");var subQ1=sQuery(id+"F0.wireOp",EDGE,"E7");Q3=makeQuery(id+"F5.boolean.opBoolean","INTERSECT",EDGE,{"derivedFrom":[makeQuery(id+"F1.opExtrude","CAP_FACE",FACE,{"disambiguationData":[OSD([subQ1,sQuery(id+"F0.wireOp",EDGE,"E10.MirrorCS"),sQuery(id+"F0.wireOp",EDGE,"E11.0"),sQuery(id+"F0.wireOp",EDGE,"E11.1"),sQuery(id+"F0.wireOp",EDGE,"E12"),sQuery(id+"F0.wireOp",EDGE,"E13.MirrorCS"),subQ0,sQuery(id+"F0.wireOp",EDGE,"E15"),sQuery(id+"F0.wireOp",EDGE,"E16"),sQuery(id+"F0.wireOp",EDGE,"E18"),sQuery(id+"F0.wireOp",EDGE,"E19"),sQuery(id+"F0.wireOp",EDGE,"E22"),sQuery(id+"F0.wireOp",EDGE,"E23"),sQuery(id+"F0.wireOp",EDGE,"E24")])],"isStart":true}),makeQuery(id+"F5.opExtrude","SWEPT_FACE",FACE,{"disambiguationData":[OSD([subQ0]),TDD([makeQuery(id+"F0.imprint","IMPRINT",EDGE,{"disambiguationData":[TD([[makeQuery(id+"F0.imprint","INTERSECT",VERTEX,{"derivedFrom":[subQ0,sQuery(id+"F0.wireOp",EDGE,"E14.right")]}),1.0]])],"derivedFrom":subQ0})])]})]});}
            var Q4;
            {var subQ0=sQuery(id+"F0.wireOp",EDGE,"E14.bottom");var subQ1=sQuery(id+"F0.wireOp",EDGE,"E10.MirrorCS");Q4=makeQuery(id+"F5.boolean.opBoolean","INTERSECT",EDGE,{"derivedFrom":[makeQuery(id+"F1.opExtrude","CAP_FACE",FACE,{"disambiguationData":[OSD([sQuery(id+"F0.wireOp",EDGE,"E7"),subQ1,sQuery(id+"F0.wireOp",EDGE,"E11.0"),sQuery(id+"F0.wireOp",EDGE,"E11.1"),sQuery(id+"F0.wireOp",EDGE,"E12"),sQuery(id+"F0.wireOp",EDGE,"E13.MirrorCS"),subQ0,sQuery(id+"F0.wireOp",EDGE,"E15"),sQuery(id+"F0.wireOp",EDGE,"E16"),sQuery(id+"F0.wireOp",EDGE,"E18"),sQuery(id+"F0.wireOp",EDGE,"E19"),sQuery(id+"F0.wireOp",EDGE,"E22"),sQuery(id+"F0.wireOp",EDGE,"E23"),sQuery(id+"F0.wireOp",EDGE,"E24")])],"isStart":true}),makeQuery(id+"F5.opExtrude","SWEPT_FACE",FACE,{"disambiguationData":[OSD([subQ0]),TDD([makeQuery(id+"F0.imprint","IMPRINT",EDGE,{"disambiguationData":[TD([[makeQuery(id+"F0.imprint","INTERSECT",VERTEX,{"derivedFrom":[subQ0,sQuery(id+"F0.wireOp",EDGE,"E14.left")]}),-1.0]])],"derivedFrom":subQ0})])]})]});}
            var Q5;
            Q5=makeQuery(id+"F5.boolean.opBoolean","INTERSECT",EDGE,{"derivedFrom":[makeQuery(id+"F1.opExtrude","CAP_FACE",FACE,{"disambiguationData":[OSD([sQuery(id+"F0.wireOp",EDGE,"E7"),sQuery(id+"F0.wireOp",EDGE,"E10.MirrorCS"),sQuery(id+"F0.wireOp",EDGE,"E11.0"),sQuery(id+"F0.wireOp",EDGE,"E11.1"),sQuery(id+"F0.wireOp",EDGE,"E12"),sQuery(id+"F0.wireOp",EDGE,"E13.MirrorCS"),sQuery(id+"F0.wireOp",EDGE,"E14.bottom"),sQuery(id+"F0.wireOp",EDGE,"E15"),sQuery(id+"F0.wireOp",EDGE,"E16"),sQuery(id+"F0.wireOp",EDGE,"E18"),sQuery(id+"F0.wireOp",EDGE,"E19"),sQuery(id+"F0.wireOp",EDGE,"E22"),sQuery(id+"F0.wireOp",EDGE,"E23"),sQuery(id+"F0.wireOp",EDGE,"E24")])],"isStart":true}),makeQuery(id+"F5.opExtrude","SWEPT_FACE",FACE,{"disambiguationData":[OSD([sQuery(id+"F0.wireOp",EDGE,"E14.left")])]})]});
            var Q6;
            Q6=makeQuery(id+"F4.opExtrude","SWEPT_EDGE",EDGE,{"disambiguationData":[OSD([sQuery(id+"F0.wireOp",EDGE,"E19"),sQuery(id+"F0.wireOp",EDGE,"E21")])]});
            var Q7;
            Q7=makeQuery(id+"F4.opExtrude","SWEPT_EDGE",EDGE,{"disambiguationData":[OSD([sQuery(id+"F0.wireOp",EDGE,"E19"),sQuery(id+"F0.wireOp",EDGE,"E20")])]});
            var Q8;
            Q8=makeQuery(id+"F4.boolean.opBoolean","SPLIT",EDGE,{"derivedFrom":makeQuery(id+"F4.opExtrude","SWEPT_EDGE",EDGE,{"disambiguationData":[OSD([sQuery(id+"F0.wireOp",EDGE,"E7"),sQuery(id+"F0.wireOp",EDGE,"E14.bottom")])]})});
            var Q9;
            Q9=makeQuery(id+"F4.boolean.opBoolean","SPLIT",EDGE,{"derivedFrom":makeQuery(id+"F4.opExtrude","SWEPT_EDGE",EDGE,{"disambiguationData":[OSD([sQuery(id+"F0.wireOp",EDGE,"E10.MirrorCS"),sQuery(id+"F0.wireOp",EDGE,"E14.bottom")])]})});
            var Q10;
            Q10=makeQuery(id+"F3.opExtrude","CAP_EDGE",EDGE,{"disambiguationData":[OSD([sQuery(id+"F0.wireOp",EDGE,"E19")])],"isStart":false});
            fillet(context, id + "F10", {"entities" : qUnion([Q0, Q1, Q2, Q3, Q4, Q5, Q6, Q7, Q8, Q9, Q10]), "radius" : 1.27 * mm, "tangentPropagation" : true, "allowEdgeOverflow" : false});
        }
    });
